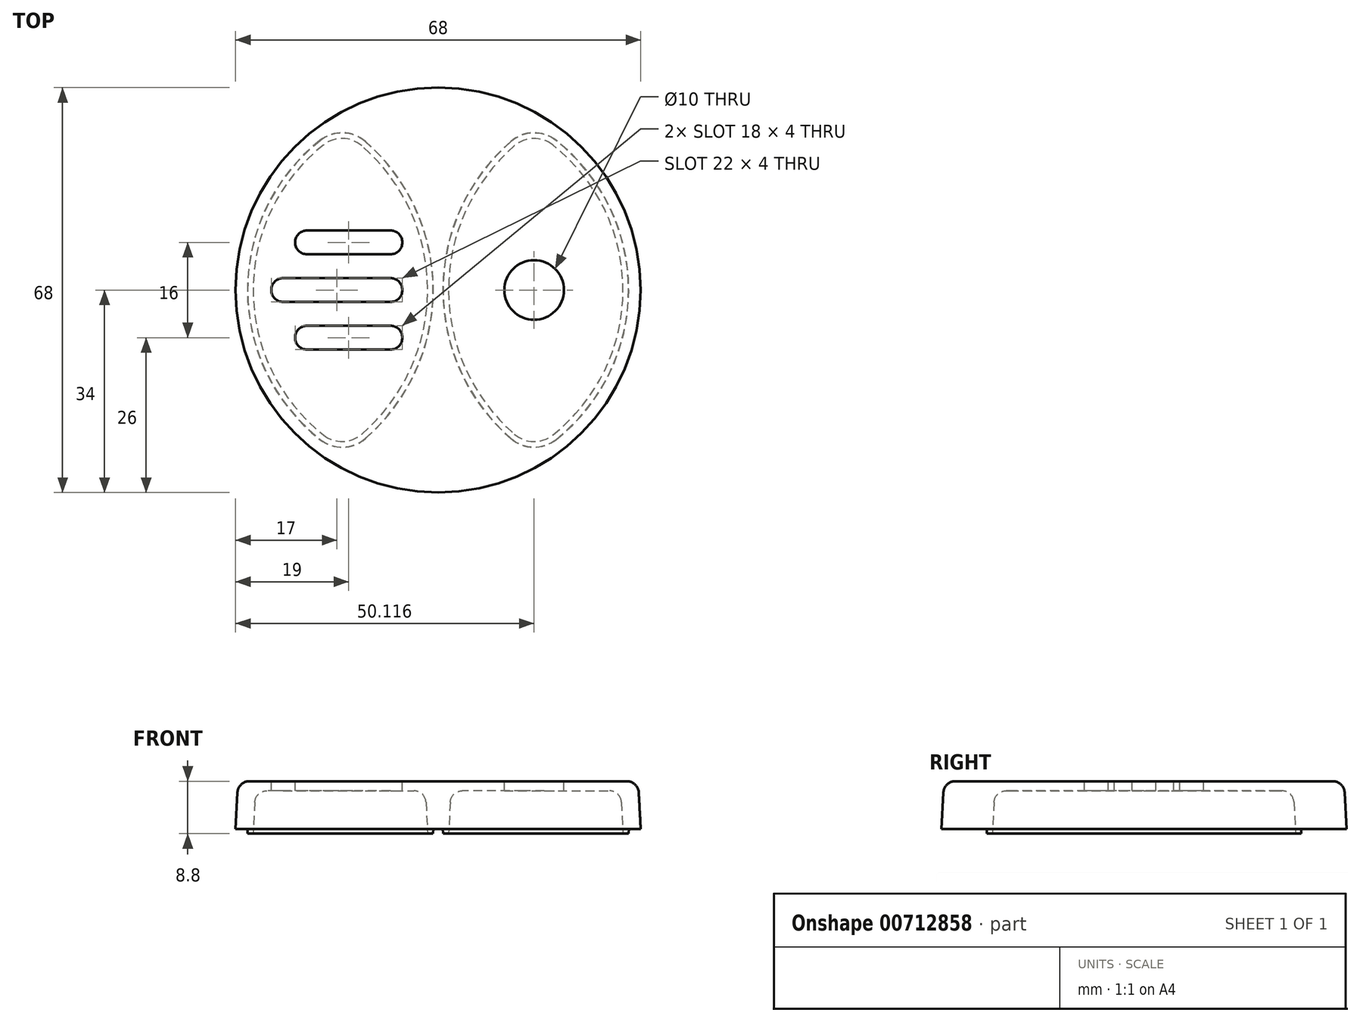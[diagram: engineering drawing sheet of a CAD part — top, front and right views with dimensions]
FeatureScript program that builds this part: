
annotation { "Feature Type Name" : "Feature", "Feature Type Description" : "" }
export const myFeature = defineFeature(function(context is Context, id is Id, definition is map)
    precondition{}
    {
        {
            var Q0;
            Q0=qCreatedBy(makeId("Top.planeOp"),FACE);
            var sketch = newSketch(context, id + "F0", { "sketchPlane" : qUnion([Q0])});
            skCircle(sketch, "E0", {"center": v(0, 0) * mm, "radius": 34 * mm});
            skSolve(sketch);
        }
        {
            var Q0;
            Q0 = qSketchRegion(id + "F0", true);
            extrude(context, id + "F1", {"entities" : qUnion([Q0]), "depth" : 8 * mm, "offsetDistance" : 25 * mm, "hasDraft" : true, "draftAngle" : 3 * degree, "draftPullDirection" : true});
        }
        {
            var Q0;
            Q0=makeQuery(id+"F1.opExtrude","CAP_FACE",FACE,{"disambiguationData":[OSD([sQuery(id+"F0.wireOp",EDGE,"E0")])],"isStart":true});
            var sketch = newSketch(context, id + "F2", { "sketchPlane" : qUnion([Q0])});
            skArc(sketch, "E1", {"start": v(-19.22, 24.33) * mm, "mid": v(-31, 0) * mm, "end": v(-19.22, -24.33) * mm});
            skArc(sketch, "E2", {"start": v(-12.84, -24.18) * mm, "mid": v(-1.8, 0) * mm, "end": v(-12.84, 24.18) * mm});
            skPoint(sketch, "E3.visualSharp", {"position": v(-15.97, 26.57) * mm});
            skArc(sketch, "E3.filletArc", {"start": v(-12.84, 24.18) * mm, "mid": v(-16, 25.4) * mm, "end": v(-19.22, 24.33) * mm});
            skPoint(sketch, "E4.visualSharp", {"position": v(-15.97, -26.57) * mm});
            skArc(sketch, "E4.filletArc", {"start": v(-19.22, -24.33) * mm, "mid": v(-16, -25.4) * mm, "end": v(-12.84, -24.18) * mm});
            skArc(sketch, "E5.MirrorCS", {"start": v(12.84, -24.18) * mm, "mid": v(1.8, 0) * mm, "end": v(12.84, 24.18) * mm});
            skArc(sketch, "E6.MirrorCS", {"start": v(12.84, 24.18) * mm, "mid": v(16, 25.4) * mm, "end": v(19.22, 24.33) * mm});
            skArc(sketch, "E7.MirrorCS", {"start": v(19.22, 24.33) * mm, "mid": v(31, 0) * mm, "end": v(19.22, -24.33) * mm});
            skArc(sketch, "E8.MirrorCS", {"start": v(19.22, -24.33) * mm, "mid": v(16, -25.4) * mm, "end": v(12.84, -24.18) * mm});
            skSolve(sketch);
        }
        {
            var Q0;
            Q0 = qSketchRegion(id + "F2", true);
            extrude(context, id + "F3", {"entities" : qUnion([Q0]), "operationType" : NewBodyOperationType.REMOVE, "oppositeDirection" : true, "depth" : (8 - 1.6) * mm, "offsetDistance" : 25 * mm, "hasDraft" : true, "draftAngle" : 3 * degree, "draftPullDirection" : true});
        }
        {
            var Q0;
            Q0=makeQuery(id+"F1.opExtrude","CAP_FACE",FACE,{"disambiguationData":[OSD([sQuery(id+"F0.wireOp",EDGE,"E0")])],"isStart":true});
            var sketch = newSketch(context, id + "F4", { "sketchPlane" : qUnion([Q0])});
            skArc(sketch, "E9.0", {"start": v(-19.22, 24.33) * mm, "mid": v(-31, 0) * mm, "end": v(-19.22, -24.33) * mm});
            skArc(sketch, "E10.0", {"start": v(-12.84, 24.18) * mm, "mid": v(-16, 25.4) * mm, "end": v(-19.22, 24.33) * mm});
            skArc(sketch, "E11.0", {"start": v(-12.84, -24.18) * mm, "mid": v(-1.8, 0) * mm, "end": v(-12.84, 24.18) * mm});
            skArc(sketch, "E12.0", {"start": v(-19.22, -24.33) * mm, "mid": v(-16, -25.4) * mm, "end": v(-12.84, -24.18) * mm});
            skArc(sketch, "E13.0", {"start": v(-12.19, 24.94) * mm, "mid": v(-15.98, 26.4) * mm, "end": v(-19.84, 25.11) * mm});
            skArc(sketch, "E13.1", {"start": v(-12.19, -24.94) * mm, "mid": v(-0.8, 0) * mm, "end": v(-12.19, 24.94) * mm});
            skArc(sketch, "E13.2", {"start": v(-19.84, -25.11) * mm, "mid": v(-15.98, -26.4) * mm, "end": v(-12.19, -24.94) * mm});
            skArc(sketch, "E13.3", {"start": v(-19.84, 25.11) * mm, "mid": v(-32, 0) * mm, "end": v(-19.84, -25.11) * mm});
            skArc(sketch, "E14.MirrorCS", {"start": v(19.84, 25.11) * mm, "mid": v(32, 0) * mm, "end": v(19.84, -25.11) * mm});
            skArc(sketch, "E15.MirrorCS", {"start": v(12.19, 24.94) * mm, "mid": v(15.98, 26.4) * mm, "end": v(19.84, 25.11) * mm});
            skArc(sketch, "E16.MirrorCS", {"start": v(12.19, -24.94) * mm, "mid": v(0.8, 0) * mm, "end": v(12.19, 24.94) * mm});
            skArc(sketch, "E17.MirrorCS", {"start": v(19.84, -25.11) * mm, "mid": v(15.98, -26.4) * mm, "end": v(12.19, -24.94) * mm});
            skArc(sketch, "E18.MirrorCS", {"start": v(19.22, 24.33) * mm, "mid": v(31, 0) * mm, "end": v(19.22, -24.33) * mm});
            skArc(sketch, "E19.MirrorCS", {"start": v(12.84, -24.18) * mm, "mid": v(1.8, 0) * mm, "end": v(12.84, 24.18) * mm});
            skArc(sketch, "E20.MirrorCS", {"start": v(12.84, 24.18) * mm, "mid": v(16, 25.4) * mm, "end": v(19.22, 24.33) * mm});
            skArc(sketch, "E21.MirrorCS", {"start": v(19.22, -24.33) * mm, "mid": v(16, -25.4) * mm, "end": v(12.84, -24.18) * mm});
            skSolve(sketch);
        }
        {
            var Q0;
            Q0 = qSketchRegion(id + "F4", true);
            extrude(context, id + "F5", {"entities" : qUnion([Q0]), "operationType" : NewBodyOperationType.ADD, "depth" : 0.8 * mm, "offsetDistance" : 25 * mm, "hasDraft" : true, "draftAngle" : 3 * degree, "draftPullDirection" : true});
        }
        {
            var Q0;
            Q0=makeQuery(id+"F1.opExtrude","CAP_EDGE",EDGE,{"disambiguationData":[OSD([sQuery(id+"F0.wireOp",EDGE,"E0")])],"isStart":false});
            var Q1;
            Q1=makeQuery(id+"F3.boolean.opBoolean","COPY",EDGE,{"derivedFrom":makeQuery(id+"F3.opExtrude","CAP_EDGE",EDGE,{"disambiguationData":[OSD([sQuery(id+"F2.wireOp",EDGE,"E1")])],"isStart":false})});
            var Q2;
            Q2=makeQuery(id+"F3.boolean.opBoolean","COPY",EDGE,{"derivedFrom":makeQuery(id+"F3.opExtrude","CAP_EDGE",EDGE,{"disambiguationData":[OSD([sQuery(id+"F2.wireOp",EDGE,"E5.MirrorCS")])],"isStart":false})});
            fillet(context, id + "F6", {"entities" : qUnion([Q0, Q1, Q2]), "radius" : 2 * mm, "tangentPropagation" : true, "allowEdgeOverflow" : false});
        }
        {
            var Q0;
            Q0=makeQuery(id+"F1.opExtrude","CAP_FACE",FACE,{"disambiguationData":[OSD([sQuery(id+"F0.wireOp",EDGE,"E0")])],"isStart":false});
            var sketch = newSketch(context, id + "F7", { "sketchPlane" : qUnion([Q0])});
            skArc(sketch, "E22.0.0", {"start": v(14.3, 22.5) * mm, "mid": v(16.05, 23.17) * mm, "end": v(17.83, 22.57) * mm, "construction": true});
            skArc(sketch, "E22.0.1", {"start": v(17.83, 22.57) * mm, "mid": v(28.77, 0) * mm, "end": v(17.83, -22.57) * mm, "construction": true});
            skArc(sketch, "E22.0.2", {"start": v(17.83, -22.57) * mm, "mid": v(16.05, -23.17) * mm, "end": v(14.3, -22.5) * mm, "construction": true});
            skArc(sketch, "E22.0.3", {"start": v(14.3, -22.5) * mm, "mid": v(4.03, 0) * mm, "end": v(14.3, 22.5) * mm, "construction": true});
            skLineSegment(sketch, "E23", {"start": v(16.12, 20.4) * mm, "end": v(16.12, -20.4) * mm, "construction": true});
            skPoint(sketch, "E24", {"position": v(16.12, 0) * mm});
            skSolve(sketch);
        }
        {
            var Q0;
            Q0=sQuery(id+"F7.wireOp",VERTEX,"E24");
            var Q1;
            Q1=makeQuery(id+"F1.opExtrude","SWEPT_BODY",BODY,{"disambiguationData":[OSD([sQuery(id+"F0.wireOp",EDGE,"E0")])]});
            hole(context, id + "F8", {"style" : HoleStyle.SIMPLE, "endStyle" : HoleEndStyle.THROUGH, "holeDiameter" : 10 * mm, "majorDiameter" : 5 * mm, "isTappedThrough" : true, "tappedDepth" : 12 * mm, "tapClearance" : 3, "locations" : qUnion([Q0]), "scope" : qUnion([Q1])});
        }
        {
            var Q0;
            Q0=makeQuery(id+"F1.opExtrude","CAP_FACE",FACE,{"disambiguationData":[OSD([sQuery(id+"F0.wireOp",EDGE,"E0")])],"isStart":false});
            var sketch = newSketch(context, id + "F9", { "sketchPlane" : qUnion([Q0])});
            skLineSegment(sketch, "E25.0.1.0", {"start": v(-8, -2) * mm, "end": v(-26, -2) * mm});
            skLineSegment(sketch, "E25.0.1.1", {"start": v(-8, 2) * mm, "end": v(-26, 2) * mm});
            skArc(sketch, "E25.0.1.2", {"start": v(-8, -2) * mm, "mid": v(-6, 0) * mm, "end": v(-8, 2) * mm});
            skArc(sketch, "E25.0.1.3", {"start": v(-26, 2) * mm, "mid": v(-28, 0) * mm, "end": v(-26, -2) * mm});
            skSolve(sketch);
        }
        {
            var Q0;
            Q0 = qSketchRegion(id + "F9", true);
            extrude(context, id + "F10", {"entities" : qUnion([Q0]), "operationType" : NewBodyOperationType.REMOVE, "endBound" : BoundingType.THROUGH_ALL, "oppositeDirection" : true, "depth" : 25 * mm, "offsetDistance" : 25 * mm});
        }
        {
            var Q0;
            Q0=makeQuery(id+"F1.opExtrude","CAP_FACE",FACE,{"disambiguationData":[OSD([sQuery(id+"F0.wireOp",EDGE,"E0")])],"isStart":false});
            var sketch = newSketch(context, id + "F11", { "sketchPlane" : qUnion([Q0])});
            skArc(sketch, "E26", {"start": v(-8, 6) * mm, "mid": v(-6, 8) * mm, "end": v(-8, 10) * mm});
            skArc(sketch, "E27", {"start": v(-22, 10) * mm, "mid": v(-24, 8) * mm, "end": v(-22, 6) * mm});
            skLineSegment(sketch, "E28", {"start": v(-22, 10) * mm, "end": v(-8, 10) * mm});
            skLineSegment(sketch, "E29", {"start": v(-22, 6) * mm, "end": v(-8, 6) * mm});
            skLineSegment(sketch, "E30", {"start": v(-8, 8) * mm, "end": v(-8, 0) * mm, "construction": true});
            skArc(sketch, "E31.MirrorCS", {"start": v(-8, -6) * mm, "mid": v(-6, -8) * mm, "end": v(-8, -10) * mm});
            skLineSegment(sketch, "E32.MirrorCS", {"start": v(-22, -10) * mm, "end": v(-8, -10) * mm});
            skLineSegment(sketch, "E33.MirrorCS", {"start": v(-22, -6) * mm, "end": v(-8, -6) * mm});
            skArc(sketch, "E34.MirrorCS", {"start": v(-22, -10) * mm, "mid": v(-24, -8) * mm, "end": v(-22, -6) * mm});
            skSolve(sketch);
        }
        {
            var Q0;
            Q0 = qSketchRegion(id + "F11", true);
            extrude(context, id + "F12", {"entities" : qUnion([Q0]), "operationType" : NewBodyOperationType.REMOVE, "endBound" : BoundingType.THROUGH_ALL, "oppositeDirection" : true, "depth" : 25 * mm, "offsetDistance" : 25 * mm});
        }
    });
